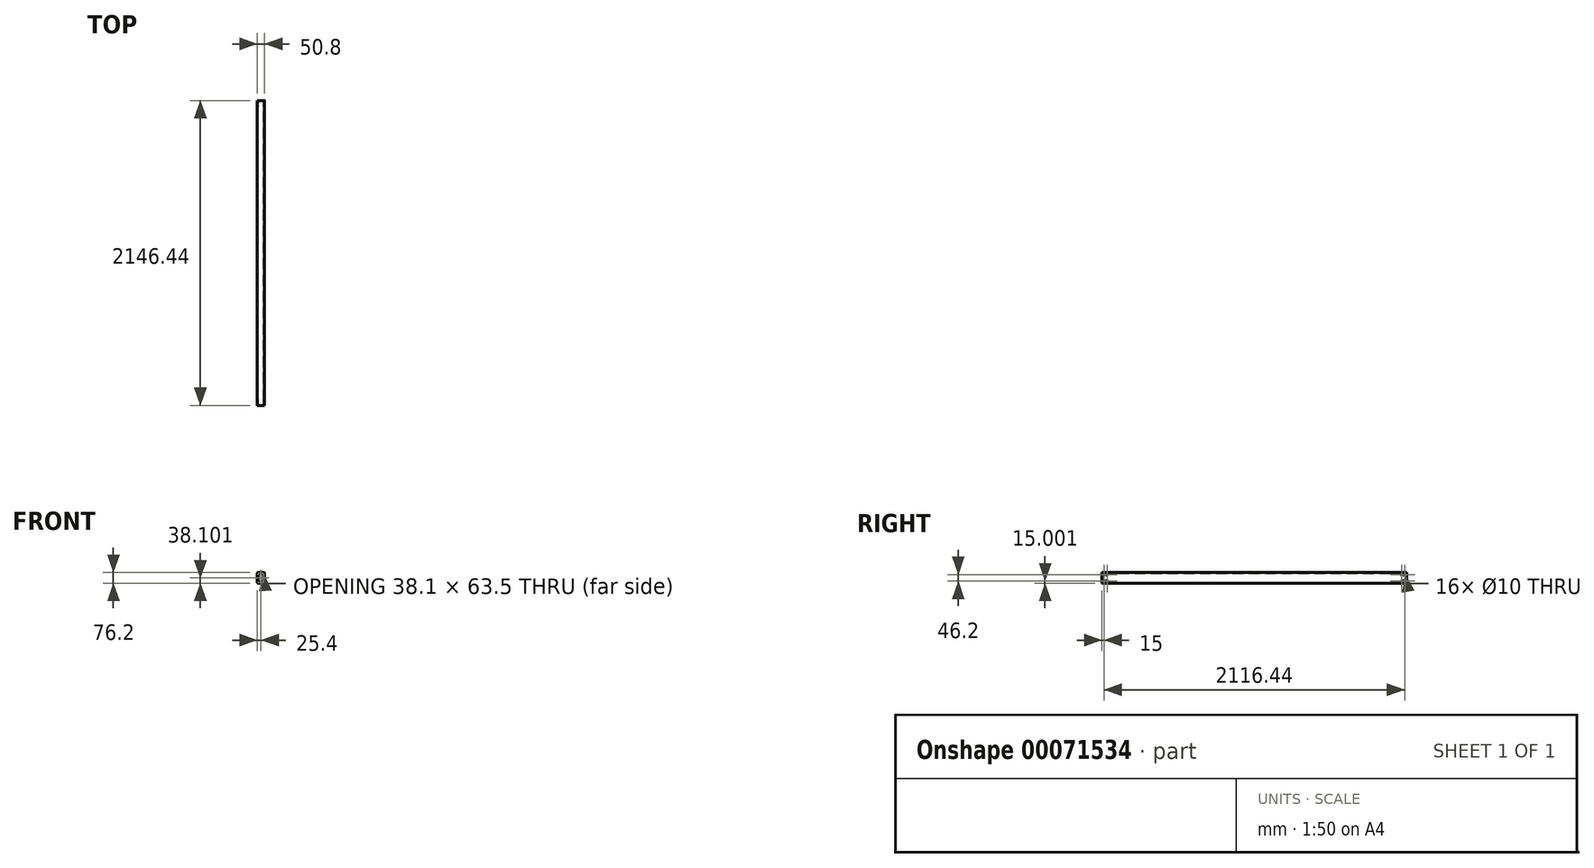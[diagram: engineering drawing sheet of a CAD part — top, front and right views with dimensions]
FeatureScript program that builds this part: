
annotation { "Feature Type Name" : "Feature", "Feature Type Description" : "" }
export const myFeature = defineFeature(function(context is Context, id is Id, definition is map)
    precondition{}
    {
        {
            var Q0;
            Q0=qCreatedBy(makeId("Front.planeOp"),FACE);
            var sketch = newSketch(context, id + "F0", { "sketchPlane" : qUnion([Q0])});
            skLineSegment(sketch, "E0.bottom", {"start": v(-12.7, 36.7) * mm, "end": v(25.4, 36.7) * mm});
            skLineSegment(sketch, "E0.top", {"start": v(-12.7, -39.5) * mm, "end": v(25.4, -39.5) * mm});
            skLineSegment(sketch, "E0.left", {"start": v(-19.05, 30.34) * mm, "end": v(-19.05, -33.16) * mm});
            skLineSegment(sketch, "E0.right", {"start": v(31.75, 30.34) * mm, "end": v(31.75, -33.16) * mm});
            skLineSegment(sketch, "E1.bottom", {"start": v(-6.35, 30.34) * mm, "end": v(19.05, 30.34) * mm});
            skLineSegment(sketch, "E1.top", {"start": v(-6.35, -33.16) * mm, "end": v(19.05, -33.16) * mm});
            skLineSegment(sketch, "E1.left", {"start": v(-12.7, 24) * mm, "end": v(-12.7, -26.8) * mm});
            skLineSegment(sketch, "E1.right", {"start": v(25.4, 24) * mm, "end": v(25.4, -26.8) * mm});
            skPoint(sketch, "E2.visualSharp", {"position": v(-12.7, 30.34) * mm});
            skArc(sketch, "E2.filletArc", {"start": v(-6.35, 30.34) * mm, "mid": v(-10.84, 28.48) * mm, "end": v(-12.7, 24) * mm});
            skPoint(sketch, "E3.visualSharp", {"position": v(25.4, 30.34) * mm});
            skArc(sketch, "E3.filletArc", {"start": v(25.4, 24) * mm, "mid": v(23.54, 28.48) * mm, "end": v(19.05, 30.34) * mm});
            skPoint(sketch, "E4.visualSharp", {"position": v(25.4, -33.16) * mm});
            skArc(sketch, "E4.filletArc", {"start": v(19.05, -33.16) * mm, "mid": v(23.54, -31.3) * mm, "end": v(25.4, -26.8) * mm});
            skPoint(sketch, "E5.visualSharp", {"position": v(-12.7, -33.16) * mm});
            skArc(sketch, "E5.filletArc", {"start": v(-12.7, -26.8) * mm, "mid": v(-10.84, -31.3) * mm, "end": v(-6.35, -33.16) * mm});
            skPoint(sketch, "E6.visualSharp", {"position": v(31.75, -39.5) * mm});
            skArc(sketch, "E6.filletArc", {"start": v(25.4, -39.5) * mm, "mid": v(29.9, -37.65) * mm, "end": v(31.75, -33.16) * mm});
            skPoint(sketch, "E7.visualSharp", {"position": v(-19.05, -39.5) * mm});
            skArc(sketch, "E7.filletArc", {"start": v(-19.05, -33.16) * mm, "mid": v(-17.2, -37.65) * mm, "end": v(-12.7, -39.5) * mm});
            skPoint(sketch, "E8.visualSharp", {"position": v(31.75, 36.7) * mm});
            skArc(sketch, "E8.filletArc", {"start": v(31.75, 30.34) * mm, "mid": v(29.9, 34.83) * mm, "end": v(25.4, 36.7) * mm});
            skPoint(sketch, "E9.visualSharp", {"position": v(-19.05, 36.7) * mm});
            skArc(sketch, "E9.filletArc", {"start": v(-12.7, 36.7) * mm, "mid": v(-17.2, 34.83) * mm, "end": v(-19.05, 30.34) * mm});
            skSolve(sketch);
        }
        {
            var Q0;
            Q0=qSketchRegion(id+"F0",true);
            extrude(context, id + "F1", {"entities" : qUnion([Q0]), "depth" : 2146.44 * mm});
        }
        {
            var Q0;
            Q0=makeQuery(id+"F1.opExtrude","SWEPT_FACE",FACE,{"disambiguationData":[OSD([sQuery(id+"F0.wireOp",EDGE,"E0.right")])]});
            var sketch = newSketch(context, id + "F2", { "sketchPlane" : qUnion([Q0])});
            skCircle(sketch, "E10", {"center": v(-2131.44, 21.7) * mm, "radius": 5 * mm});
            skCircle(sketch, "E11", {"center": v(-2110.64, 21.7) * mm, "radius": 5 * mm});
            skCircle(sketch, "E12", {"center": v(-2131.44, -24.5) * mm, "radius": 5 * mm});
            skCircle(sketch, "E13", {"center": v(-2110.64, -24.5) * mm, "radius": 5 * mm});
            skCircle(sketch, "E14", {"center": v(-35.8, 21.7) * mm, "radius": 5 * mm});
            skCircle(sketch, "E15.0.1.0", {"center": v(-35.8, -24.5) * mm, "radius": 5 * mm});
            skCircle(sketch, "E15.1.0.0", {"center": v(-15, 21.7) * mm, "radius": 5 * mm});
            skCircle(sketch, "E15.1.1.0", {"center": v(-15, -24.5) * mm, "radius": 5 * mm});
            skLineSegment(sketch, "E15.direction1", {"start": v(-35.8, 21.7) * mm, "end": v(-15, 21.7) * mm, "construction": true});
            skLineSegment(sketch, "E15.direction2", {"start": v(-35.8, 21.7) * mm, "end": v(-35.8, -24.5) * mm, "construction": true});
            skSolve(sketch);
        }
        {
            var Q0;
            Q0 = qSketchRegion(id + "F2", true);
            extrude(context, id + "F3", {"entities" : qUnion([Q0]), "operationType" : NewBodyOperationType.REMOVE, "endBound" : BoundingType.THROUGH_ALL, "oppositeDirection" : true, "depth" : 25 * mm});
        }
    });
